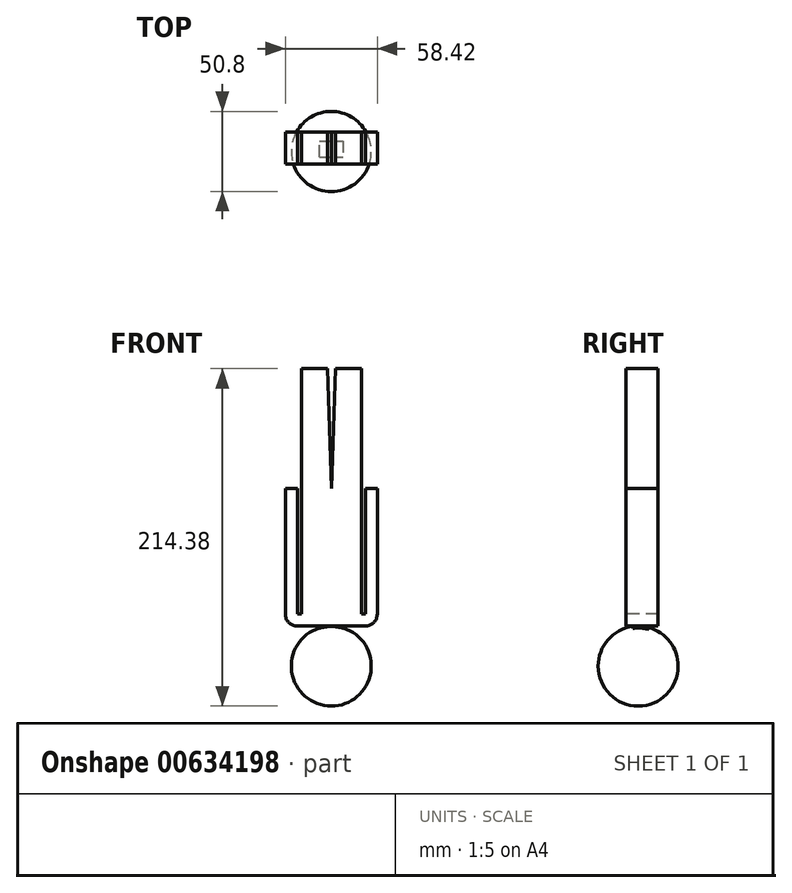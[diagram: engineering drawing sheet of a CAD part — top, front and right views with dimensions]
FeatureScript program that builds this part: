
annotation { "Feature Type Name" : "Feature", "Feature Type Description" : "" }
export const myFeature = defineFeature(function(context is Context, id is Id, definition is map)
    precondition{}
    {
        {
            var Q0;
            Q0=qCreatedBy(makeId("Front.planeOp"),FACE);
            var sketch = newSketch(context, id + "F0", { "sketchPlane" : qUnion([Q0])});
            skCircle(sketch, "E0", {"center": v(0, 0) * mm, "radius": 25.4 * mm});
            skSolve(sketch);
        }
        {
            var Q0;
            Q0 = qSketchRegion(id + "F0", true);
            extrude(context, id + "F1", {"entities" : qUnion([Q0]), "depth" : 50.8 * mm, "offsetDistance" : 25.4 * mm});
        }
        {
            var Q0;
            Q0=makeQuery(id+"F1.opExtrude","CAP_EDGE",EDGE,{"disambiguationData":[OSD([sQuery(id+"F0.wireOp",EDGE,"E0")])],"isStart":false});
            fillet(context, id + "F2", {"entities" : qUnion([Q0]), "radius" : 25.4 * mm, "tangentPropagation" : true, "allowEdgeOverflow" : false});
        }
        {
            var Q0;
            Q0=makeQuery(id+"F1.opExtrude","CAP_FACE",FACE,{"disambiguationData":[OSD([sQuery(id+"F0.wireOp",EDGE,"E0")])],"isStart":true});
            fillet(context, id + "F3", {"entities" : qUnion([Q0]), "radius" : 25.4 * mm, "tangentPropagation" : true, "allowEdgeOverflow" : false});
        }
        {
            var Q0;
            Q0=qCreatedBy(makeId("Top.planeOp"),FACE);
            var sketch = newSketch(context, id + "F4", { "sketchPlane" : qUnion([Q0])});
            skLineSegment(sketch, "E1.bottom", {"start": v(0, -18.7) * mm, "end": v(7.62, -18.7) * mm});
            skLineSegment(sketch, "E1.top", {"start": v(0, -28.86) * mm, "end": v(7.62, -28.86) * mm});
            skLineSegment(sketch, "E1.left", {"start": v(0, -18.7) * mm, "end": v(0, -28.86) * mm});
            skLineSegment(sketch, "E1.right", {"start": v(7.62, -18.7) * mm, "end": v(7.62, -28.86) * mm});
            skLineSegment(sketch, "E2.bottom", {"start": v(0, -28.86) * mm, "end": v(-7.62, -28.86) * mm});
            skLineSegment(sketch, "E2.top", {"start": v(0, -18.7) * mm, "end": v(-7.62, -18.7) * mm});
            skLineSegment(sketch, "E2.left", {"start": v(0, -28.86) * mm, "end": v(0, -18.7) * mm});
            skLineSegment(sketch, "E2.right", {"start": v(-7.62, -28.86) * mm, "end": v(-7.62, -18.7) * mm});
            skSolve(sketch);
        }
        {
            var Q0;
            Q0 = qSketchRegion(id + "F4", true);
            extrude(context, id + "F5", {"entities" : qUnion([Q0]), "operationType" : NewBodyOperationType.ADD, "depth" : 50.8 * mm, "offsetDistance" : 25.4 * mm});
        }
        {
            var Q0;
            Q0=makeQuery(id+"F5.opExtrude","CAP_FACE",FACE,{"disambiguationData":[OSD([sQuery(id+"F4.wireOp",EDGE,"E1.bottom"),sQuery(id+"F4.wireOp",EDGE,"E1.top"),sQuery(id+"F4.wireOp",EDGE,"E1.right"),sQuery(id+"F4.wireOp",EDGE,"E2.bottom"),sQuery(id+"F4.wireOp",EDGE,"E2.top"),sQuery(id+"F4.wireOp",EDGE,"E2.right")])],"isStart":false});
            var sketch = newSketch(context, id + "F6", { "sketchPlane" : qUnion([Q0])});
            skLineSegment(sketch, "E3.bottom", {"start": v(7.62, -18.7) * mm, "end": v(29.21, -18.7) * mm});
            skLineSegment(sketch, "E3.top", {"start": v(7.62, -33.25) * mm, "end": v(29.21, -33.25) * mm});
            skLineSegment(sketch, "E3.left", {"start": v(7.62, -18.7) * mm, "end": v(7.62, -33.25) * mm});
            skLineSegment(sketch, "E3.right", {"start": v(29.21, -18.7) * mm, "end": v(29.21, -33.25) * mm});
            skLineSegment(sketch, "E4.bottom", {"start": v(29.21, -33.25) * mm, "end": v(-29.21, -33.25) * mm});
            skLineSegment(sketch, "E4.top", {"start": v(29.21, -12.93) * mm, "end": v(-29.21, -12.93) * mm});
            skLineSegment(sketch, "E4.left", {"start": v(29.21, -33.25) * mm, "end": v(29.21, -12.93) * mm});
            skLineSegment(sketch, "E4.right", {"start": v(-29.21, -33.25) * mm, "end": v(-29.21, -12.93) * mm});
            skLineSegment(sketch, "E5", {"start": v(-7.62, -18.7) * mm, "end": v(-29.21, -18.7) * mm});
            skSolve(sketch);
        }
        {
            var Q0;
            Q0 = qSketchRegion(id + "F6", true);
            extrude(context, id + "F7", {"entities" : qUnion([Q0]), "operationType" : NewBodyOperationType.ADD, "depth" : 61.98 * mm, "offsetDistance" : 25.4 * mm, "hasSecondDirection" : true, "secondDirectionOppositeDirection" : true, "secondDirectionDepth" : 25.4 * mm});
        }
        {
            var Q0;
            Q0=makeQuery(id+"F7.opExtrude","CAP_EDGE",EDGE,{"disambiguationData":[OSD([sQuery(id+"F6.wireOp",EDGE,"E4.left")])],"isStart":true});
            fillet(context, id + "F8", {"entities" : qUnion([Q0]), "radius" : 7.62 * mm, "tangentPropagation" : true, "allowEdgeOverflow" : false});
        }
        {
            var Q0;
            Q0=makeQuery(id+"F7.opExtrude","CAP_EDGE",EDGE,{"disambiguationData":[OSD([sQuery(id+"F6.wireOp",EDGE,"E4.right")])],"isStart":true});
            fillet(context, id + "F9", {"entities" : qUnion([Q0]), "radius" : 7.62 * mm, "tangentPropagation" : true, "allowEdgeOverflow" : false});
        }
        {
            var Q0;
            Q0=makeQuery(id+"F7.opExtrude","SWEPT_FACE",FACE,{"disambiguationData":[OSD([sQuery(id+"F6.wireOp",EDGE,"E4.bottom")])]});
            var sketch = newSketch(context, id + "F10", { "sketchPlane" : qUnion([Q0])});
            skLineSegment(sketch, "E6", {"start": v(21.59, 33.02) * mm, "end": v(21.59, 112.78) * mm});
            skLineSegment(sketch, "E7", {"start": v(21.59, 112.78) * mm, "end": v(-21.6, 112.78) * mm});
            skLineSegment(sketch, "E8", {"start": v(-21.6, 112.78) * mm, "end": v(-21.6, 33.02) * mm});
            skLineSegment(sketch, "E9.bottom", {"start": v(21.59, 33.02) * mm, "end": v(19.05, 33.02) * mm});
            skLineSegment(sketch, "E9.top", {"start": v(21.59, 112.78) * mm, "end": v(19.05, 112.78) * mm});
            skLineSegment(sketch, "E9.right", {"start": v(19.05, 33.02) * mm, "end": v(19.05, 112.78) * mm});
            skLineSegment(sketch, "E10.bottom", {"start": v(-21.6, 33.02) * mm, "end": v(-19.05, 33.02) * mm});
            skLineSegment(sketch, "E10.top", {"start": v(-21.6, 112.78) * mm, "end": v(-19.05, 112.78) * mm});
            skLineSegment(sketch, "E10.left", {"start": v(-21.6, 33.02) * mm, "end": v(-21.6, 112.78) * mm});
            skLineSegment(sketch, "E10.right", {"start": v(-19.05, 33.02) * mm, "end": v(-19.05, 112.78) * mm});
            skSolve(sketch);
        }
        {
            var Q0;
            Q0 = qSketchRegion(id + "F10", true);
            extrude(context, id + "F11", {"entities" : qUnion([Q0]), "operationType" : NewBodyOperationType.REMOVE, "oppositeDirection" : true, "depth" : 25.4 * mm, "offsetDistance" : 25.4 * mm});
        }
        {
            var Q0;
            {var subQ0=sQuery(id+"F6.wireOp",EDGE,"E4.bottom");var subQ1=sQuery(id+"F6.wireOp",EDGE,"E4.top");Q0=makeQuery(id+"F11.boolean.opBoolean","SPLIT",FACE,{"disambiguationData":[TD([makeQuery(id+"F11.opExtrude","SWEPT_FACE",FACE,{"disambiguationData":[OSD([sQuery(id+"F10.wireOp",EDGE,"E9.right")])]})])],"derivedFrom":makeQuery(id+"F7.opExtrude","CAP_FACE",FACE,{"disambiguationData":[OSD([subQ0,subQ1,sQuery(id+"F6.wireOp",EDGE,"E4.left"),sQuery(id+"F6.wireOp",EDGE,"E4.right")])],"isStart":false})});}
            var sketch = newSketch(context, id + "F12", { "sketchPlane" : qUnion([Q0])});
            skLineSegment(sketch, "E11.bottom", {"start": v(19.05, -33.25) * mm, "end": v(-19.05, -33.25) * mm});
            skLineSegment(sketch, "E11.top", {"start": v(19.05, -12.93) * mm, "end": v(-19.05, -12.93) * mm});
            skLineSegment(sketch, "E11.left", {"start": v(19.05, -33.25) * mm, "end": v(19.05, -12.93) * mm});
            skLineSegment(sketch, "E11.right", {"start": v(-19.05, -33.25) * mm, "end": v(-19.05, -12.93) * mm});
            skSolve(sketch);
        }
        {
            var Q0;
            Q0 = qSketchRegion(id + "F12", true);
            extrude(context, id + "F13", {"entities" : qUnion([Q0]), "operationType" : NewBodyOperationType.ADD, "depth" : 76.2 * mm, "offsetDistance" : 25.4 * mm});
        }
        {
            var Q0;
            Q0=makeQuery(id+"F13.boolean.opBoolean","MERGE",FACE,{"derivedFrom":[makeQuery(id+"F7.opExtrude","SWEPT_FACE",FACE,{"disambiguationData":[OSD([sQuery(id+"F6.wireOp",EDGE,"E4.top")])]}),makeQuery(id+"F13.opExtrude","SWEPT_FACE",FACE,{"disambiguationData":[OSD([sQuery(id+"F12.wireOp",EDGE,"E11.top")])]})]});
            var sketch = newSketch(context, id + "F14", { "sketchPlane" : qUnion([Q0])});
            skLineSegment(sketch, "E12", {"start": v(0, 112.78) * mm, "end": v(0, 188.98) * mm});
            skLineSegment(sketch, "E13", {"start": v(0, 188.98) * mm, "end": v(-2.54, 188.98) * mm});
            skLineSegment(sketch, "E14", {"start": v(-2.54, 188.98) * mm, "end": v(0, 112.78) * mm});
            skLineSegment(sketch, "E15", {"start": v(0, 188.98) * mm, "end": v(2.54, 188.98) * mm});
            skLineSegment(sketch, "E16", {"start": v(2.54, 188.98) * mm, "end": v(0, 112.78) * mm});
            skSolve(sketch);
        }
        {
            var Q0;
            Q0 = qSketchRegion(id + "F14", true);
            extrude(context, id + "F15", {"entities" : qUnion([Q0]), "operationType" : NewBodyOperationType.REMOVE, "oppositeDirection" : true, "depth" : 25.4 * mm, "offsetDistance" : 25.4 * mm});
        }
    });
